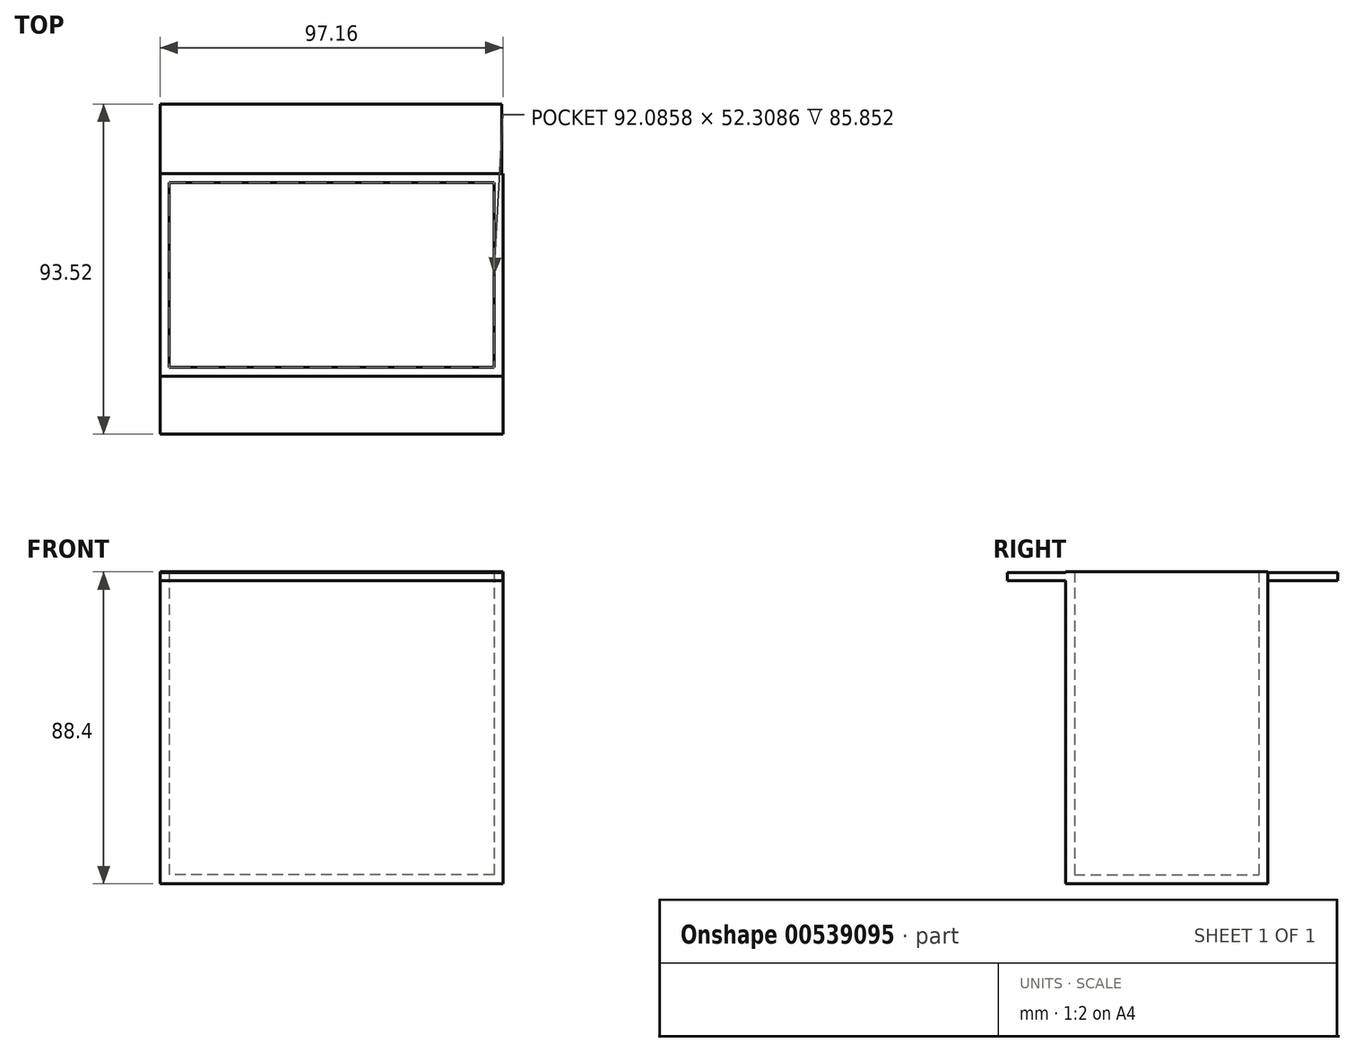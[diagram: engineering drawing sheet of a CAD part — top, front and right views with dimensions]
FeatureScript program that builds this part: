
annotation { "Feature Type Name" : "Feature", "Feature Type Description" : "" }
export const myFeature = defineFeature(function(context is Context, id is Id, definition is map)
    precondition{}
    {
        {
            var Q0;
            Q0=qCreatedBy(makeId("Top.planeOp"),FACE);
            var sketch = newSketch(context, id + "F0", { "sketchPlane" : qUnion([Q0])});
            skLineSegment(sketch, "E0.bottom", {"start": v(48.58, -28.7) * mm, "end": v(-48.58, -28.7) * mm});
            skLineSegment(sketch, "E0.top", {"start": v(48.58, 28.7) * mm, "end": v(-48.58, 28.7) * mm});
            skLineSegment(sketch, "E0.left", {"start": v(48.58, -28.7) * mm, "end": v(48.58, 28.7) * mm});
            skLineSegment(sketch, "E0.right", {"start": v(-48.58, -28.7) * mm, "end": v(-48.58, 28.7) * mm});
            skPoint(sketch, "E0.middle", {"position": v(0, 0) * mm});
            skSolve(sketch);
        }
        {
            var Q0;
            Q0 = qSketchRegion(id + "F0", true);
            extrude(context, id + "F1", {"entities" : qUnion([Q0]), "depth" : 44.2 * mm, "offsetDistance" : 25.4 * mm, "hasSecondDirection" : true, "secondDirectionOppositeDirection" : true, "secondDirectionDepth" : 44.2 * mm});
        }
        {
            var Q0;
            Q0=qCreatedBy(makeId("Top.planeOp"),FACE);
            var sketch = newSketch(context, id + "F2", { "sketchPlane" : qUnion([Q0])});
            skLineSegment(sketch, "E1.bottom", {"start": v(-48.58, 28.7) * mm, "end": v(48.28, 28.7) * mm});
            skLineSegment(sketch, "E1.top", {"start": v(-48.58, 48.43) * mm, "end": v(48.28, 48.43) * mm});
            skLineSegment(sketch, "E1.left", {"start": v(-48.58, 28.7) * mm, "end": v(-48.58, 48.43) * mm});
            skLineSegment(sketch, "E1.right", {"start": v(48.28, 28.7) * mm, "end": v(48.28, 48.43) * mm});
            skSolve(sketch);
        }
        {
            var Q0;
            Q0=qCreatedBy(makeId("Top.planeOp"),FACE);
            var sketch = newSketch(context, id + "F3", { "sketchPlane" : qUnion([Q0])});
            skLineSegment(sketch, "E2.bottom", {"start": v(-48.58, -28.7) * mm, "end": v(48.58, -28.7) * mm});
            skLineSegment(sketch, "E2.top", {"start": v(-48.58, -45.1) * mm, "end": v(48.58, -45.1) * mm});
            skLineSegment(sketch, "E2.left", {"start": v(-48.58, -28.7) * mm, "end": v(-48.58, -45.1) * mm});
            skLineSegment(sketch, "E2.right", {"start": v(48.58, -28.7) * mm, "end": v(48.58, -45.1) * mm});
            skSolve(sketch);
        }
        {
            var Q0;
            Q0=makeQuery(id+"F1.opExtrude","CAP_FACE",FACE,{"disambiguationData":[OSD([sQuery(id+"F0.wireOp",EDGE,"E0.bottom"),sQuery(id+"F0.wireOp",EDGE,"E0.top"),sQuery(id+"F0.wireOp",EDGE,"E0.left"),sQuery(id+"F0.wireOp",EDGE,"E0.right")])],"isStart":false});
            shell(context, id + "F4", {"entities" : qUnion([Q0]), "thickness" : 2.54 * mm});
        }
        {
            var Q0;
            Q0=makeQuery(id+"F2.imprint","IMPRINT",FACE,{"disambiguationData":[TD([[makeQuery(id+"F2.imprint","IMPRINT",EDGE,{"derivedFrom":sQuery(id+"F2.wireOp",EDGE,"E1.bottom")}),1.0]])]});
            var Q1;
            Q1=makeQuery(id+"F3.imprint","IMPRINT",FACE,{"disambiguationData":[TD([[makeQuery(id+"F3.imprint","IMPRINT",EDGE,{"derivedFrom":sQuery(id+"F3.wireOp",EDGE,"E2.bottom")}),-1.0]])]});
            extrude(context, id + "F5", {"entities" : qUnion([Q0, Q1]), "operationType" : NewBodyOperationType.ADD, "depth" : 43.94 * mm, "offsetDistance" : 25.4 * mm, "hasSecondDirection" : true, "secondDirectionOppositeDirection" : false, "secondDirectionDepth" : 41.66 * mm});
        }
    });
